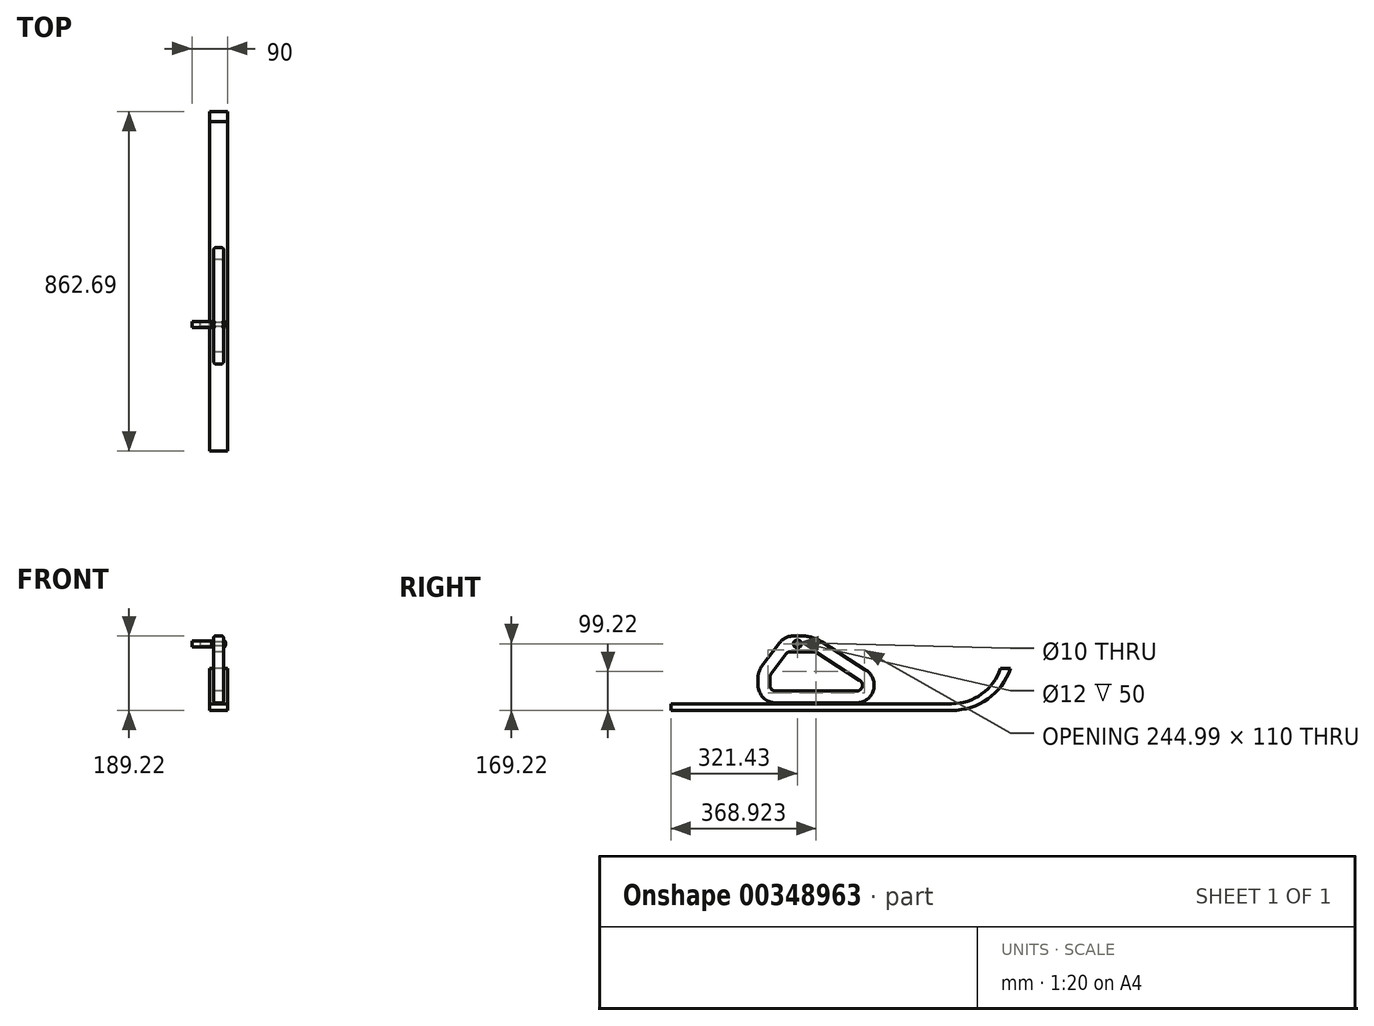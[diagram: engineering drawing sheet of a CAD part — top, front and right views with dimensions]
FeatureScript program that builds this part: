
annotation { "Feature Type Name" : "Feature", "Feature Type Description" : "" }
export const myFeature = defineFeature(function(context is Context, id is Id, definition is map)
    precondition{}
    {
        {
            var Q0;
            Q0=qCreatedBy(makeId("Right.planeOp"),FACE);
            var sketch = newSketch(context, id + "F0", { "sketchPlane" : qUnion([Q0])});
            skCircle(sketch, "E0", {"center": v(0, 0) * mm, "radius": 8 * mm});
            skCircle(sketch, "E1", {"center": v(0, 0) * mm, "radius": 6 * mm});
            skSolve(sketch);
        }
        {
            var Q0;
            Q0=makeQuery(id+"F0.imprint","IMPRINT",FACE,{"disambiguationData":[TD([[makeQuery(id+"F0.imprint","IMPRINT",EDGE,{"derivedFrom":sQuery(id+"F0.wireOp",EDGE,"E0")}),1.0]])]});
            extrude(context, id + "F1", {"entities" : qUnion([Q0]), "oppositeDirection" : true, "depth" : 50 * mm});
        }
        {
            var Q0;
            Q0=qCreatedBy(makeId("Right.planeOp"),FACE);
            var sketch = newSketch(context, id + "F2", { "sketchPlane" : qUnion([Q0])});
            skLineSegment(sketch, "E2", {"start": v(0, 0) * mm, "end": v(0, 20) * mm, "construction": true});
            skLineSegment(sketch, "E3", {"start": v(-10, 20) * mm, "end": v(0, 20) * mm});
            skLineSegment(sketch, "E4", {"start": v(-46, 2) * mm, "end": v(-91, -58) * mm});
            skLineSegment(sketch, "E5", {"start": v(-100, -85) * mm, "end": v(-100, -105) * mm});
            skLineSegment(sketch, "E6", {"start": v(-55, -150) * mm, "end": v(0, -150) * mm});
            skLineSegment(sketch, "E7", {"start": v(0, -120) * mm, "end": v(-55, -120) * mm});
            skLineSegment(sketch, "E8", {"start": v(-70, -105) * mm, "end": v(-70, -85) * mm});
            skLineSegment(sketch, "E9", {"start": v(-67, -76) * mm, "end": v(-29.5, -26) * mm});
            skLineSegment(sketch, "E10", {"start": v(-17.5, -20) * mm, "end": v(0, -20) * mm});
            skArc(sketch, "E11.filletArc", {"start": v(-67, -76) * mm, "mid": v(-69.23, -80.26) * mm, "end": v(-70, -85) * mm});
            skArc(sketch, "E12.filletArc", {"start": v(-70, -105) * mm, "mid": v(-65.6, -115.6) * mm, "end": v(-55, -120) * mm});
            skArc(sketch, "E13.filletArc", {"start": v(-91, -58) * mm, "mid": v(-97.7, -70.77) * mm, "end": v(-100, -85) * mm});
            skArc(sketch, "E14.filletArc", {"start": v(-100, -105) * mm, "mid": v(-86.82, -136.82) * mm, "end": v(-55, -150) * mm});
            skArc(sketch, "E15.filletArc", {"start": v(-17.5, -20) * mm, "mid": v(-24.2, -21.58) * mm, "end": v(-29.5, -26) * mm});
            skArc(sketch, "E16.filletArc", {"start": v(-10, 20) * mm, "mid": v(-30.12, 15.25) * mm, "end": v(-46, 2) * mm});
            skLineSegment(sketch, "E17", {"start": v(0, 20) * mm, "end": v(10, 20) * mm});
            skLineSegment(sketch, "E18", {"start": v(62.12, 4.74) * mm, "end": v(174.27, -67.1) * mm});
            skLineSegment(sketch, "E19", {"start": v(150, -150) * mm, "end": v(0, -150) * mm});
            skLineSegment(sketch, "E20", {"start": v(0, -120) * mm, "end": v(150, -120) * mm});
            skLineSegment(sketch, "E21", {"start": v(158.1, -92.37) * mm, "end": v(48.82, -22.37) * mm});
            skLineSegment(sketch, "E22", {"start": v(40.73, -20) * mm, "end": v(0, -20) * mm});
            skArc(sketch, "E23.filletArc", {"start": v(150, -120) * mm, "mid": v(164.4, -109.22) * mm, "end": v(158.1, -92.37) * mm});
            skArc(sketch, "E24.filletArc", {"start": v(150, -150) * mm, "mid": v(193.19, -117.65) * mm, "end": v(174.27, -67.1) * mm});
            skArc(sketch, "E25.filletArc", {"start": v(62.12, 4.74) * mm, "mid": v(37.15, 16.1) * mm, "end": v(10, 20) * mm});
            skArc(sketch, "E26.filletArc", {"start": v(48.82, -22.37) * mm, "mid": v(44.94, -20.6) * mm, "end": v(40.73, -20) * mm});
            skCircle(sketch, "E27", {"center": v(0, 0) * mm, "radius": 5 * mm});
            skSolve(sketch);
        }
        {
            var Q0;
            Q0=makeQuery(id+"F2.imprint","IMPRINT",FACE,{"disambiguationData":[TD([[makeQuery(id+"F2.imprint","IMPRINT",EDGE,{"derivedFrom":sQuery(id+"F2.wireOp",EDGE,"E3")}),-1.0]])]});
            extrude(context, id + "F3", {"entities" : qUnion([Q0]), "depth" : 30 * mm, "hasSecondDirection" : true, "secondDirectionOppositeDirection" : false, "secondDirectionDepth" : 5 * mm});
        }
        {
            var Q0;
            Q0=qCreatedBy(makeId("Right.planeOp"),FACE);
            var sketch = newSketch(context, id + "F4", { "sketchPlane" : qUnion([Q0])});
            skLineSegment(sketch, "E28.bottom", {"start": v(-321.43, -152.29) * mm, "end": v(391.45, -152.29) * mm});
            skLineSegment(sketch, "E28.top", {"start": v(-321.43, -169.22) * mm, "end": v(391.45, -169.22) * mm});
            skLineSegment(sketch, "E28.left", {"start": v(-321.43, -152.29) * mm, "end": v(-321.43, -169.22) * mm});
            skLineSegment(sketch, "E28.right", {"start": v(391.45, -152.29) * mm, "end": v(391.45, -169.22) * mm});
            skArc(sketch, "E29", {"start": v(391.45, -152.29) * mm, "mid": v(467.94, -127.6) * mm, "end": v(515.55, -62.86) * mm});
            skArc(sketch, "E30", {"start": v(391.45, -169.22) * mm, "mid": v(483.32, -139.92) * mm, "end": v(541.26, -62.86) * mm});
            skLineSegment(sketch, "E31", {"start": v(515.55, -62.86) * mm, "end": v(541.26, -62.86) * mm});
            skSolve(sketch);
        }
        {
            var Q0;
            Q0=makeQuery(id+"F4.imprint","IMPRINT",FACE,{"disambiguationData":[TD([[makeQuery(id+"F4.imprint","IMPRINT",EDGE,{"derivedFrom":sQuery(id+"F4.wireOp",EDGE,"E28.bottom")}),-1.0]])]});
            var Q1;
            Q1=makeQuery(id+"F4.imprint","IMPRINT",FACE,{"disambiguationData":[TD([[makeQuery(id+"F4.imprint","IMPRINT",EDGE,{"derivedFrom":sQuery(id+"F4.wireOp",EDGE,"E28.right")}),1.0]])]});
            extrude(context, id + "F5", {"entities" : qUnion([Q0, Q1]), "depth" : 40 * mm, "hasSecondDirection" : true, "secondDirectionOppositeDirection" : true, "secondDirectionDepth" : 5 * mm});
        }
        {
            var Q0;
            Q0=qCreatedBy(makeId("Top.planeOp"),FACE);
            var sketch = newSketch(context, id + "F6", { "sketchPlane" : qUnion([Q0])});
            skLineSegment(sketch, "E32", {"start": v(-29.5, 0) * mm, "end": v(35.5, 0) * mm});
            skArc(sketch, "E33", {"start": v(35.5, 0) * mm, "mid": v(34.18, 5.6) * mm, "end": v(30.5, 10) * mm});
            skLineSegment(sketch, "E34", {"start": v(30.5, 10) * mm, "end": v(30.5, 5) * mm});
            skLineSegment(sketch, "E35", {"start": v(30.5, 5) * mm, "end": v(-29.5, 5) * mm});
            skLineSegment(sketch, "E36", {"start": v(-29.5, 5) * mm, "end": v(-29.5, 0) * mm});
            skSolve(sketch);
        }
        {
            var Q0;
            Q0=makeQuery(id+"F6.imprint","IMPRINT",FACE,{"disambiguationData":[TD([[makeQuery(id+"F6.imprint","IMPRINT",EDGE,{"derivedFrom":sQuery(id+"F6.wireOp",EDGE,"E32")}),1.0]])]});
            var Q1;
            Q1=sQuery(id+"F6.wireOp",EDGE,"E32");
            revolve(context, id + "F7", {"entities" : qUnion([Q0]), "axis" : qUnion([Q1]), "revolveType" : RevolveType.FULL});
        }
        {
            var Q0;
            Q0=makeQuery(id+"F3.opExtrude","SWEPT_FACE",FACE,{"disambiguationData":[OSD([sQuery(id+"F2.wireOp",EDGE,"E16.filletArc")])]});
            var Q1;
            Q1=makeQuery(id+"F3.opExtrude","CAP_FACE",FACE,{"disambiguationData":[OSD([sQuery(id+"F2.wireOp",EDGE,"E3"),sQuery(id+"F2.wireOp",EDGE,"E4"),sQuery(id+"F2.wireOp",EDGE,"E5"),sQuery(id+"F2.wireOp",EDGE,"E6"),sQuery(id+"F2.wireOp",EDGE,"E7"),sQuery(id+"F2.wireOp",EDGE,"E8"),sQuery(id+"F2.wireOp",EDGE,"E9"),sQuery(id+"F2.wireOp",EDGE,"E10"),sQuery(id+"F2.wireOp",EDGE,"E11.filletArc"),sQuery(id+"F2.wireOp",EDGE,"E12.filletArc"),sQuery(id+"F2.wireOp",EDGE,"E13.filletArc"),sQuery(id+"F2.wireOp",EDGE,"E14.filletArc"),sQuery(id+"F2.wireOp",EDGE,"E15.filletArc"),sQuery(id+"F2.wireOp",EDGE,"E16.filletArc"),sQuery(id+"F2.wireOp",EDGE,"E17"),sQuery(id+"F2.wireOp",EDGE,"E18"),sQuery(id+"F2.wireOp",EDGE,"E19"),sQuery(id+"F2.wireOp",EDGE,"E20"),sQuery(id+"F2.wireOp",EDGE,"E21"),sQuery(id+"F2.wireOp",EDGE,"E22"),sQuery(id+"F2.wireOp",EDGE,"E23.filletArc"),sQuery(id+"F2.wireOp",EDGE,"E24.filletArc"),sQuery(id+"F2.wireOp",EDGE,"E25.filletArc"),sQuery(id+"F2.wireOp",EDGE,"E26.filletArc"),sQuery(id+"F2.wireOp",EDGE,"E27")])],"isStart":false});
            var Q2;
            Q2=makeQuery(id+"F3.opExtrude","CAP_FACE",FACE,{"disambiguationData":[OSD([sQuery(id+"F2.wireOp",EDGE,"E3"),sQuery(id+"F2.wireOp",EDGE,"E4"),sQuery(id+"F2.wireOp",EDGE,"E5"),sQuery(id+"F2.wireOp",EDGE,"E6"),sQuery(id+"F2.wireOp",EDGE,"E7"),sQuery(id+"F2.wireOp",EDGE,"E8"),sQuery(id+"F2.wireOp",EDGE,"E9"),sQuery(id+"F2.wireOp",EDGE,"E10"),sQuery(id+"F2.wireOp",EDGE,"E11.filletArc"),sQuery(id+"F2.wireOp",EDGE,"E12.filletArc"),sQuery(id+"F2.wireOp",EDGE,"E13.filletArc"),sQuery(id+"F2.wireOp",EDGE,"E14.filletArc"),sQuery(id+"F2.wireOp",EDGE,"E15.filletArc"),sQuery(id+"F2.wireOp",EDGE,"E16.filletArc"),sQuery(id+"F2.wireOp",EDGE,"E17"),sQuery(id+"F2.wireOp",EDGE,"E18"),sQuery(id+"F2.wireOp",EDGE,"E19"),sQuery(id+"F2.wireOp",EDGE,"E20"),sQuery(id+"F2.wireOp",EDGE,"E21"),sQuery(id+"F2.wireOp",EDGE,"E22"),sQuery(id+"F2.wireOp",EDGE,"E23.filletArc"),sQuery(id+"F2.wireOp",EDGE,"E24.filletArc"),sQuery(id+"F2.wireOp",EDGE,"E25.filletArc"),sQuery(id+"F2.wireOp",EDGE,"E26.filletArc"),sQuery(id+"F2.wireOp",EDGE,"E27")])],"isStart":true});
            fillet(context, id + "F8", {"entities" : qUnion([Q0, Q1, Q2]), "radius" : 5 * mm, "tangentPropagation" : true, "allowEdgeOverflow" : false});
        }
    });
